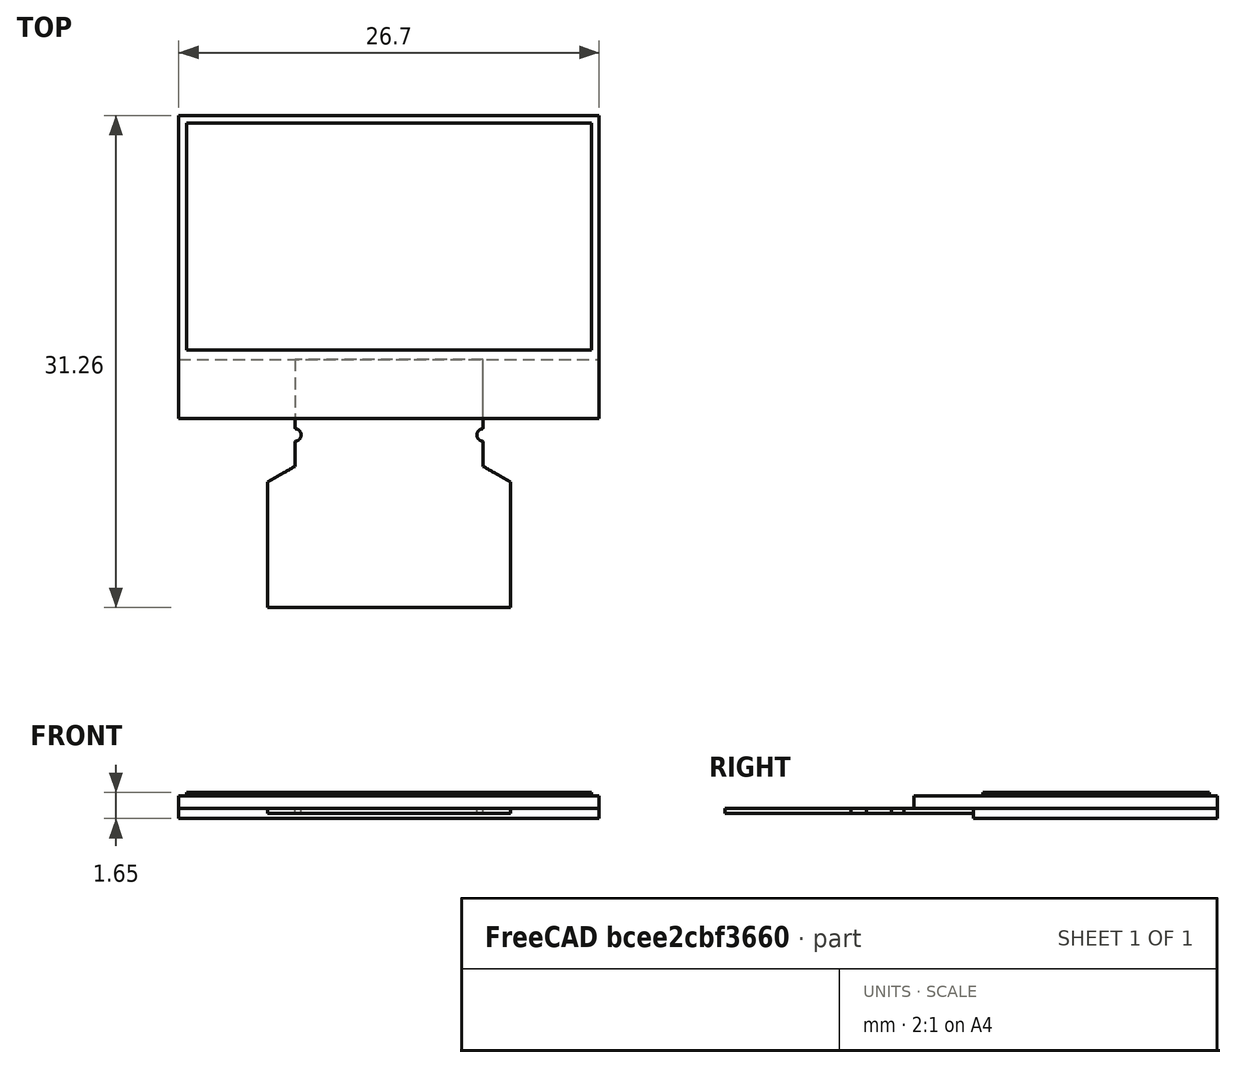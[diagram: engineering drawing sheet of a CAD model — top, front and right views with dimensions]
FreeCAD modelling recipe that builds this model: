
FCSTD DOCUMENT  (FreeCAD 0.18R16131 (Git))
Label: oled - Copy
License: All rights reserved
LicenseURL: http://en.wikipedia.org/wiki/All_rights_reserved
objects: Part::Box×3, Part::Feature×1, App::DocumentObjectGroup×1
note: 4 computed .brp shape members not serialized (recipe doc carries the construction recipe); baked Part::Feature solids carry a one-line shape summary decoded from their .brp

FEATURE [Part::Box] Box  label="Panel"
  AttacherType = Attacher::AttachEngine3D
  Height = 0.817773
  Length = 26.7
  Placement = pos=(0,0,0.632227) rot=(0,0,1;0rad)
  Width = 19.26
FEATURE [Part::Box] Box001  label="Polarizer"
  AttacherType = Attacher::AttachEngine3D
  Height = 0.2
  Length = 25.7
  Placement = pos=(0.5,4.36,1.45) rot=(0,0,1;0rad)
  Width = 14.4
FEATURE [Part::Box] Box002  label="Cap"
  AttacherType = Attacher::AttachEngine3D
  Height = 0.632227
  Length = 26.7
  Placement = pos=(0,3.76,0) rot=(0,0,1;0rad)
  Width = 15.5
FEATURE [Part::Feature] Extrude001  label="Ribbon"
  Placement = pos=(5.63,3.76,0.333) rot=(0,0,1;0rad)
  shape: bbox 15.44 x 15.76 x 0.3 mm, 16 faces (baked)
FEATURE [App::DocumentObjectGroup] Group
  Group = -> [Box001,Box,Box002,Extrude001]
